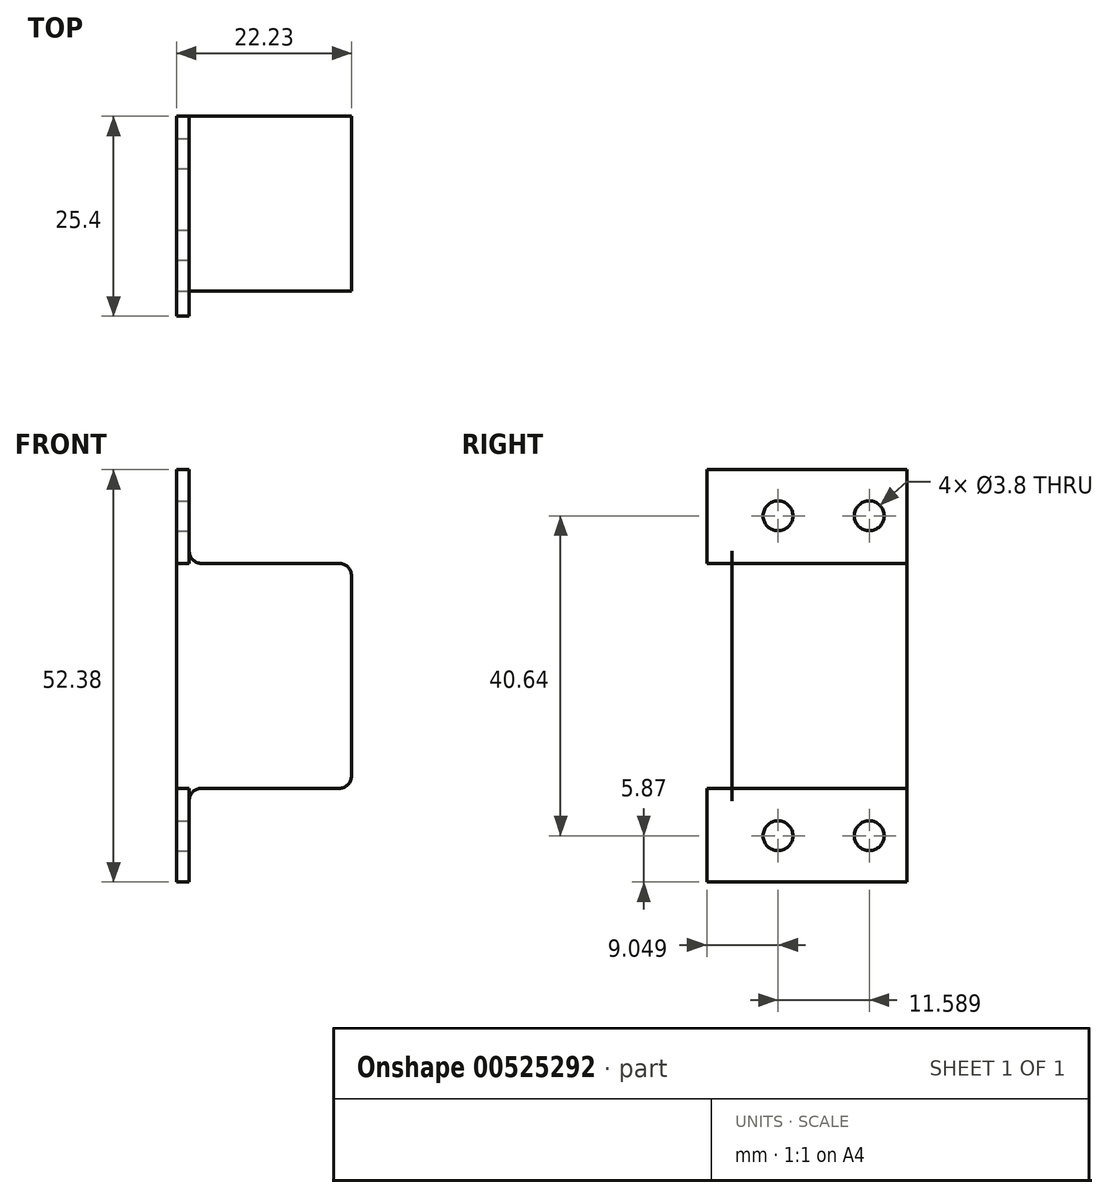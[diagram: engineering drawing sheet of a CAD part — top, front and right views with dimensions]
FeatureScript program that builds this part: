
annotation { "Feature Type Name" : "Feature", "Feature Type Description" : "" }
export const myFeature = defineFeature(function(context is Context, id is Id, definition is map)
    precondition{}
    {
        {
            var Q0;
            Q0=qCreatedBy(makeId("Front.planeOp"),FACE);
            var sketch = newSketch(context, id + "F0", { "sketchPlane" : qUnion([Q0])});
            skLineSegment(sketch, "E0", {"start": v(0, 0) * mm, "end": v(0, 26.2) * mm});
            skLineSegment(sketch, "E1", {"start": v(0, 26.2) * mm, "end": v(1.59, 26.2) * mm});
            skLineSegment(sketch, "E2", {"start": v(1.59, 26.2) * mm, "end": v(1.59, 14.29) * mm});
            skLineSegment(sketch, "E3", {"start": v(1.59, 14.29) * mm, "end": v(22.23, 14.29) * mm});
            skLineSegment(sketch, "E4", {"start": v(22.23, 14.29) * mm, "end": v(22.23, 0) * mm});
            skLineSegment(sketch, "E5.MirrorCS", {"start": v(22.23, -14.29) * mm, "end": v(22.23, 0) * mm});
            skLineSegment(sketch, "E6.MirrorCS", {"start": v(1.59, -14.29) * mm, "end": v(22.23, -14.29) * mm});
            skLineSegment(sketch, "E7.MirrorCS", {"start": v(1.59, -26.2) * mm, "end": v(1.59, -14.29) * mm});
            skLineSegment(sketch, "E8.MirrorCS", {"start": v(0, -26.2) * mm, "end": v(1.59, -26.2) * mm});
            skLineSegment(sketch, "E9.MirrorCS", {"start": v(0, 0) * mm, "end": v(0, -26.2) * mm});
            skSolve(sketch);
        }
        {
            var Q0;
            Q0 = qSketchRegion(id + "F0", true);
            extrude(context, id + "F1", {"entities" : qUnion([Q0]), "depth" : 25.4 * mm, "offsetDistance" : 25.4 * mm});
        }
        {
            var Q0;
            Q0=makeQuery(id+"F1.opExtrude","SWEPT_FACE",FACE,{"disambiguationData":[OSD([sQuery(id+"F0.wireOp",EDGE,"E2")])]});
            var sketch = newSketch(context, id + "F2", { "sketchPlane" : qUnion([Q0])});
            skLineSegment(sketch, "E10", {"start": v(-37.8, 20.32) * mm, "end": v(15.27, 20.32) * mm, "construction": true});
            skLineSegment(sketch, "E11", {"start": v(-16.35, 37.47) * mm, "end": v(-16.35, 7.24) * mm, "construction": true});
            skLineSegment(sketch, "E12", {"start": v(-4.76, 37.47) * mm, "end": v(-4.76, 7.24) * mm, "construction": true});
            skPoint(sketch, "E13", {"position": v(-16.35, 20.32) * mm});
            skPoint(sketch, "E14", {"position": v(-4.76, 20.32) * mm});
            skPoint(sketch, "E15.MirrorP", {"position": v(-16.35, -20.32) * mm});
            skPoint(sketch, "E16.MirrorP", {"position": v(-4.76, -20.32) * mm});
            skSolve(sketch);
        }
        {
            var Q0;
            Q0=sQuery(id+"F2.wireOp",VERTEX,"E13");
            var Q1;
            Q1=sQuery(id+"F2.wireOp",VERTEX,"E14");
            var Q2;
            Q2=sQuery(id+"F2.wireOp",VERTEX,"E15.MirrorP");
            var Q3;
            Q3=sQuery(id+"F2.wireOp",VERTEX,"E16.MirrorP");
            var Q4;
            Q4=makeQuery(id+"F1.opExtrude","SWEPT_BODY",BODY,{"disambiguationData":[OSD([sQuery(id+"F0.wireOp",EDGE,"E0"),sQuery(id+"F0.wireOp",EDGE,"E1"),sQuery(id+"F0.wireOp",EDGE,"E2"),sQuery(id+"F0.wireOp",EDGE,"E3"),sQuery(id+"F0.wireOp",EDGE,"E4"),sQuery(id+"F0.wireOp",EDGE,"E5.MirrorCS"),sQuery(id+"F0.wireOp",EDGE,"E6.MirrorCS"),sQuery(id+"F0.wireOp",EDGE,"E7.MirrorCS"),sQuery(id+"F0.wireOp",EDGE,"E8.MirrorCS"),sQuery(id+"F0.wireOp",EDGE,"E9.MirrorCS")])]});
            hole(context, id + "F3", {"style" : HoleStyle.SIMPLE, "endStyle" : HoleEndStyle.THROUGH, "standardTappedOrClearance" : lookupTablePath({ "standard" : "ANSI", "fit" : "Normal (ASME)", "size" : "#6", "type" : "Clearance" }), "standardBlindInLast" : lookupTablePath({ "fit" : "Free", "standard" : "ANSI", "size" : "#6", "type" : "Clearance" }), "holeDiameter" : 3.8 * mm, "isTappedThrough" : true, "tappedDepth" : 12.7 * mm, "tapClearance" : 3, "locations" : qUnion([Q0, Q1, Q2, Q3]), "scope" : qUnion([Q4])});
        }
        {
            var Q0;
            Q0=makeQuery(id+"F1.opExtrude","SWEPT_FACE",FACE,{"disambiguationData":[OSD([sQuery(id+"F0.wireOp",EDGE,"E4"),sQuery(id+"F0.wireOp",EDGE,"E5.MirrorCS")])]});
            var sketch = newSketch(context, id + "F4", { "sketchPlane" : qUnion([Q0])});
            skLineSegment(sketch, "E17.bottom", {"start": v(-25.4, 14.29) * mm, "end": v(-22.23, 14.29) * mm});
            skLineSegment(sketch, "E17.top", {"start": v(-25.4, -14.29) * mm, "end": v(-22.23, -14.29) * mm});
            skLineSegment(sketch, "E17.left", {"start": v(-25.4, 14.29) * mm, "end": v(-25.4, -14.29) * mm});
            skLineSegment(sketch, "E17.right", {"start": v(-22.23, 14.29) * mm, "end": v(-22.23, -14.29) * mm});
            skSolve(sketch);
        }
        {
            var Q0;
            Q0 = qSketchRegion(id + "F4", true);
            extrude(context, id + "F5", {"entities" : qUnion([Q0]), "operationType" : NewBodyOperationType.REMOVE, "endBound" : BoundingType.THROUGH_ALL, "oppositeDirection" : true, "depth" : 25.4 * mm, "offsetDistance" : 25.4 * mm});
        }
        {
            var Q0;
            Q0=makeQuery(id+"F1.opExtrude","SWEPT_EDGE",EDGE,{"disambiguationData":[OSD([sQuery(id+"F0.wireOp",EDGE,"E3"),sQuery(id+"F0.wireOp",EDGE,"E4")])]});
            var Q1;
            Q1=makeQuery(id+"F1.opExtrude","SWEPT_EDGE",EDGE,{"disambiguationData":[OSD([sQuery(id+"F0.wireOp",EDGE,"E5.MirrorCS"),sQuery(id+"F0.wireOp",EDGE,"E6.MirrorCS")])]});
            var Q2;
            {var subQ0=sQuery(id+"F0.wireOp",EDGE,"E2");var subQ1=sQuery(id+"F0.wireOp",EDGE,"E3");Q2=makeQuery(id+"F5.boolean.opBoolean","SPLIT",EDGE,{"disambiguationData":[topologyDisambiguationEdgeConnected([makeQuery(id+"F1.opExtrude","SWEPT_FACE",FACE,{"disambiguationData":[OSD([subQ1])]})])],"derivedFrom":makeQuery(id+"F1.opExtrude","SWEPT_EDGE",EDGE,{"disambiguationData":[OSD([subQ0,subQ1])]})});}
            var Q3;
            {var subQ0=sQuery(id+"F0.wireOp",EDGE,"E6.MirrorCS");var subQ1=sQuery(id+"F0.wireOp",EDGE,"E7.MirrorCS");Q3=makeQuery(id+"F5.boolean.opBoolean","SPLIT",EDGE,{"disambiguationData":[topologyDisambiguationEdgeConnected([makeQuery(id+"F1.opExtrude","SWEPT_FACE",FACE,{"disambiguationData":[OSD([subQ0])]})])],"derivedFrom":makeQuery(id+"F1.opExtrude","SWEPT_EDGE",EDGE,{"disambiguationData":[OSD([subQ0,subQ1])]})});}
            fillet(context, id + "F6", {"entities" : qUnion([Q0, Q1, Q2, Q3]), "radius" : 1.59 * mm, "tangentPropagation" : true, "allowEdgeOverflow" : false});
        }
    });
